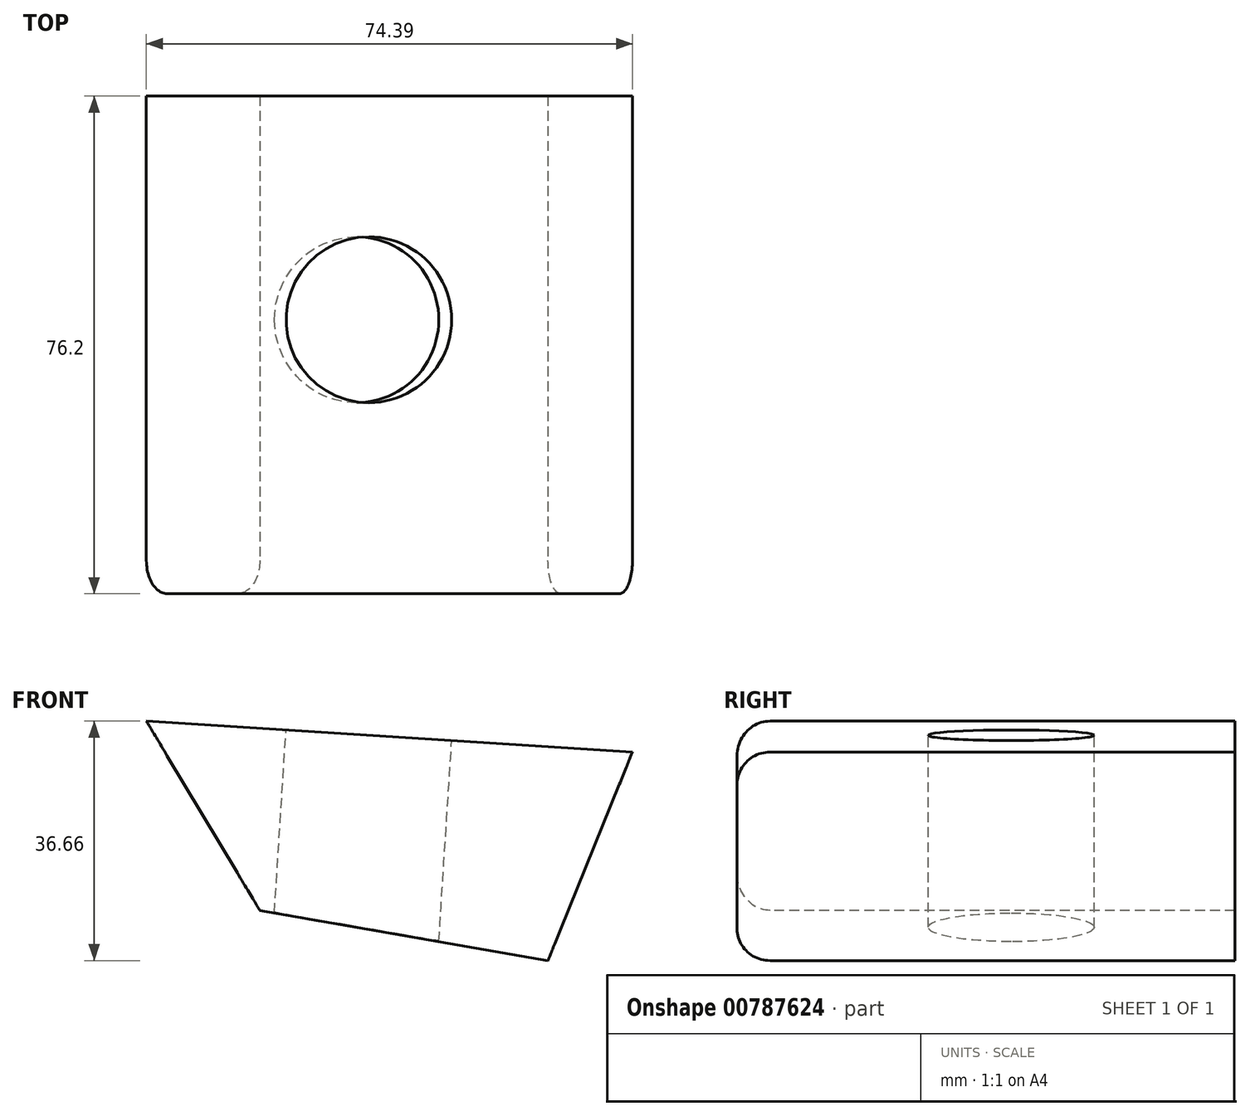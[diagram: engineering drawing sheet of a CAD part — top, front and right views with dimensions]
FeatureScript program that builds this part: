
annotation { "Feature Type Name" : "Feature", "Feature Type Description" : "" }
export const myFeature = defineFeature(function(context is Context, id is Id, definition is map)
    precondition{}
    {
        {
            var Q0;
            Q0=qCreatedBy(makeId("Front.planeOp"),FACE);
            var sketch = newSketch(context, id + "F0", { "sketchPlane" : qUnion([Q0])});
            skLineSegment(sketch, "E0", {"start": v(-61.46, 56.82) * mm, "end": v(-44.1, 27.83) * mm});
            skLineSegment(sketch, "E1", {"start": v(-44.1, 27.83) * mm, "end": v(0, 20.16) * mm});
            skLineSegment(sketch, "E2", {"start": v(0, 20.16) * mm, "end": v(12.93, 52.09) * mm});
            skLineSegment(sketch, "E3", {"start": v(-61.46, 56.82) * mm, "end": v(12.93, 52.09) * mm});
            skSolve(sketch);
        }
        {
            var Q0;
            Q0=makeQuery(id+"F0.imprint","IMPRINT",FACE,{"disambiguationData":[TD([[makeQuery(id+"F0.imprint","IMPRINT",EDGE,{"derivedFrom":sQuery(id+"F0.wireOp",EDGE,"E0")}),1.0]])]});
            extrude(context, id + "F1", {"entities" : qUnion([Q0]), "oppositeDirection" : true, "depth" : 76.2 * mm, "offsetDistance" : 25.4 * mm});
        }
        {
            var Q0;
            Q0=makeQuery(id+"F1.opExtrude","CAP_EDGE",EDGE,{"disambiguationData":[OSD([sQuery(id+"F0.wireOp",EDGE,"E3")])],"isStart":true});
            fillet(context, id + "F2", {"entities" : qUnion([Q0]), "radius" : 5.08 * mm, "tangentPropagation" : true, "allowEdgeOverflow" : false});
        }
        {
            var Q0;
            Q0=makeQuery(id+"F1.opExtrude","CAP_EDGE",EDGE,{"disambiguationData":[OSD([sQuery(id+"F0.wireOp",EDGE,"E1")])],"isStart":true});
            fillet(context, id + "F3", {"entities" : qUnion([Q0]), "radius" : 5.08 * mm, "tangentPropagation" : true, "allowEdgeOverflow" : false});
        }
        {
            var Q0;
            Q0=makeQuery(id+"F1.opExtrude","SWEPT_FACE",FACE,{"disambiguationData":[OSD([sQuery(id+"F0.wireOp",EDGE,"E3")])]});
            var sketch = newSketch(context, id + "F4", { "sketchPlane" : qUnion([Q0])});
            skCircle(sketch, "E4", {"center": v(-30.83, 41.95) * mm, "radius": 11.69 * mm});
            skSolve(sketch);
        }
        {
            var Q0;
            Q0=sQuery(id+"F4.wireOp",VERTEX,"E4.center");
            var Q1;
            Q1=makeQuery(id+"F1.opExtrude","SWEPT_BODY",BODY,{"disambiguationData":[OSD([sQuery(id+"F0.wireOp",EDGE,"E0"),sQuery(id+"F0.wireOp",EDGE,"E1"),sQuery(id+"F0.wireOp",EDGE,"E2"),sQuery(id+"F0.wireOp",EDGE,"E3")])]});
            hole(context, id + "F5", {"style" : HoleStyle.SIMPLE, "endStyle" : HoleEndStyle.THROUGH, "holeDiameter" : 25.4 * mm, "majorDiameter" : 6.35 * mm, "isTappedThrough" : true, "tappedDepth" : 12.7 * mm, "tapClearance" : 3, "locations" : qUnion([Q0]), "scope" : qUnion([Q1])});
        }
    });
